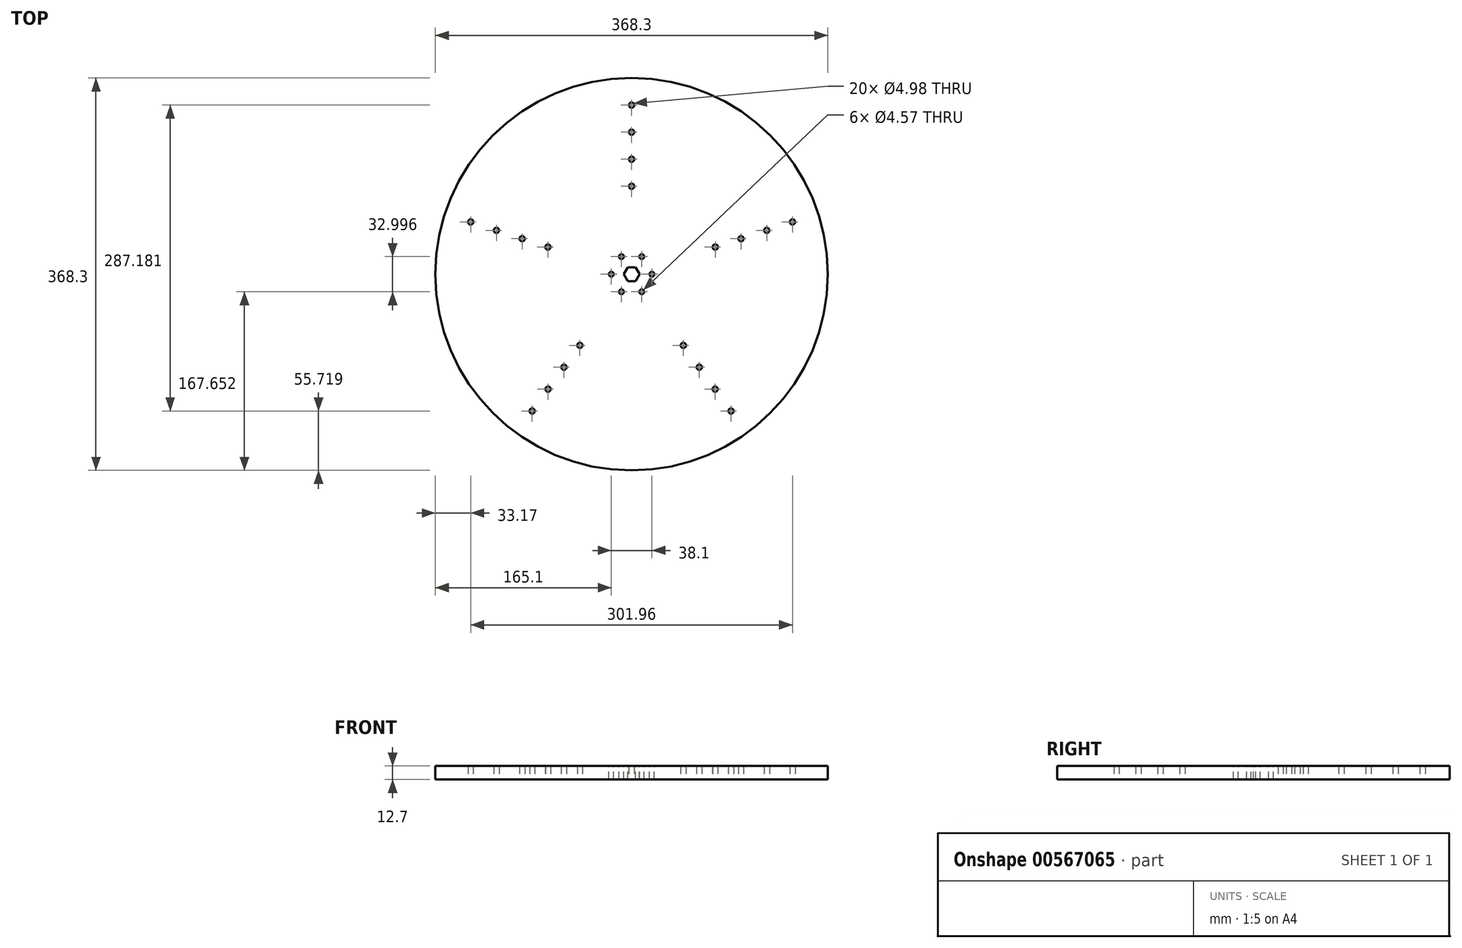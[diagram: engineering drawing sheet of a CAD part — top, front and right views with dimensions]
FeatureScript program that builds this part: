
annotation { "Feature Type Name" : "Feature", "Feature Type Description" : "" }
export const myFeature = defineFeature(function(context is Context, id is Id, definition is map)
    precondition{}
    {
        {
            var Q0;
            Q0=qCreatedBy(makeId("Top.planeOp"),FACE);
            var sketch = newSketch(context, id + "F0", { "sketchPlane" : qUnion([Q0])});
            skLineSegment(sketch, "E0", {"start": v(-174.54, 58.71) * mm, "end": v(-174.54, 58.71) * mm});
            skArc(sketch, "E1.cCircle", {"start": v(-174.54, 58.71) * mm, "mid": v(-175.72, -55.1) * mm, "end": v(-109.78, -147.85) * mm});
            skLineSegment(sketch, "E1.0", {"start": v(133.8, -184.15) * mm, "end": v(-133.8, -184.15) * mm, "construction": true});
            skLineSegment(sketch, "E1.1", {"start": v(-133.8, -184.15) * mm, "end": v(-216.48, 70.34) * mm, "construction": true});
            skLineSegment(sketch, "E1.2", {"start": v(-216.48, 70.34) * mm, "end": v(0, 227.62) * mm, "construction": true});
            skLineSegment(sketch, "E1.3", {"start": v(0, 227.62) * mm, "end": v(216.48, 70.34) * mm, "construction": true});
            skLineSegment(sketch, "E1.4", {"start": v(216.48, 70.34) * mm, "end": v(133.8, -184.15) * mm, "construction": true});
            skPoint(sketch, "E1.0.midPoint", {"position": v(0, -184.15) * mm});
            skLineSegment(sketch, "E2", {"start": v(0, 227.62) * mm, "end": v(0, 0) * mm, "construction": true});
            skLineSegment(sketch, "E3", {"start": v(-216.48, 70.34) * mm, "end": v(0, 0) * mm, "construction": true});
            skLineSegment(sketch, "E4", {"start": v(-133.8, -184.15) * mm, "end": v(0, 0) * mm, "construction": true});
            skLineSegment(sketch, "E5", {"start": v(133.8, -184.15) * mm, "end": v(0, 0) * mm, "construction": true});
            skLineSegment(sketch, "E6", {"start": v(216.48, 70.34) * mm, "end": v(0, 0) * mm, "construction": true});
            skLineSegment(sketch, "E7.bottom", {"start": v(1.9, 57.15) * mm, "end": v(-1.9, 57.15) * mm, "construction": true});
            skLineSegment(sketch, "E7.top", {"start": v(1.9, 209.55) * mm, "end": v(-1.9, 209.55) * mm, "construction": true});
            skLineSegment(sketch, "E7.left", {"start": v(1.9, 57.15) * mm, "end": v(1.9, 209.55) * mm, "construction": true});
            skLineSegment(sketch, "E7.right", {"start": v(-1.9, 57.15) * mm, "end": v(-1.9, 209.55) * mm, "construction": true});
            skArc(sketch, "E8.trimOffspring", {"start": v(-109.78, -147.85) * mm, "mid": v(175.72, 55.1) * mm, "end": v(-174.54, 58.71) * mm});
            skCircle(sketch, "E9", {"center": v(0, 82.55) * mm, "radius": 2.49 * mm});
            skCircle(sketch, "E10.0.1.0", {"center": v(0, 107.95) * mm, "radius": 2.49 * mm});
            skCircle(sketch, "E10.0.2.0", {"center": v(0, 133.35) * mm, "radius": 2.49 * mm});
            skLineSegment(sketch, "E10.direction1", {"start": v(0, 82.55) * mm, "end": v(25.4, 82.55) * mm, "construction": true});
            skLineSegment(sketch, "E10.direction2", {"start": v(0, 82.55) * mm, "end": v(0, 107.95) * mm, "construction": true});
            skCircle(sketch, "E11.0.0.3", {"center": v(0, 158.75) * mm, "radius": 2.49 * mm});
            skCircle(sketch, "E12.1.0", {"center": v(-78.5, 25.5) * mm, "radius": 2.49 * mm});
            skCircle(sketch, "E12.1.1", {"center": v(-102.67, 33.36) * mm, "radius": 2.49 * mm});
            skCircle(sketch, "E12.1.2", {"center": v(-126.82, 41.2) * mm, "radius": 2.49 * mm});
            skCircle(sketch, "E12.1.3", {"center": v(-150.98, 49.06) * mm, "radius": 2.49 * mm});
            skCircle(sketch, "E12.2.0", {"center": v(-48.52, -66.78) * mm, "radius": 2.49 * mm});
            skCircle(sketch, "E12.2.1", {"center": v(-63.45, -87.33) * mm, "radius": 2.49 * mm});
            skCircle(sketch, "E12.2.2", {"center": v(-78.38, -107.88) * mm, "radius": 2.49 * mm});
            skCircle(sketch, "E12.2.3", {"center": v(-93.31, -128.43) * mm, "radius": 2.49 * mm});
            skCircle(sketch, "E12.3.0", {"center": v(48.52, -66.78) * mm, "radius": 2.49 * mm});
            skCircle(sketch, "E12.3.1", {"center": v(63.45, -87.33) * mm, "radius": 2.49 * mm});
            skCircle(sketch, "E12.3.2", {"center": v(78.38, -107.88) * mm, "radius": 2.49 * mm});
            skCircle(sketch, "E12.3.3", {"center": v(93.31, -128.43) * mm, "radius": 2.49 * mm});
            skCircle(sketch, "E12.4.0", {"center": v(78.5, 25.5) * mm, "radius": 2.49 * mm});
            skCircle(sketch, "E12.4.1", {"center": v(102.67, 33.36) * mm, "radius": 2.49 * mm});
            skCircle(sketch, "E12.4.2", {"center": v(126.82, 41.2) * mm, "radius": 2.49 * mm});
            skCircle(sketch, "E12.4.3", {"center": v(150.98, 49.06) * mm, "radius": 2.49 * mm});
            skLineSegment(sketch, "E13", {"start": v(-1.9, 177.8) * mm, "end": v(1.9, 177.8) * mm, "construction": true});
            skSolve(sketch);
        }
        {
            var Q0;
            Q0=makeQuery(id+"F0.imprint","IMPRINT",FACE,{"disambiguationData":[TD([[makeQuery(id+"F0.imprint","IMPRINT",EDGE,{"derivedFrom":sQuery(id+"F0.wireOp",EDGE,"E1.cCircle")}),1.0]])]});
            extrude(context, id + "F1", {"entities" : qUnion([Q0]), "depth" : 12.7 * mm, "offsetDistance" : 25.4 * mm});
        }
        {
            var Q0;
            Q0=makeQuery(id+"F1.opExtrude","CAP_FACE",FACE,{"disambiguationData":[OSD([sQuery(id+"F0.wireOp",EDGE,"E1.cCircle"),sQuery(id+"F0.wireOp",EDGE,"E8.trimOffspring"),sQuery(id+"F0.wireOp",EDGE,"E9"),sQuery(id+"F0.wireOp",EDGE,"E10.0.1.0"),sQuery(id+"F0.wireOp",EDGE,"E10.0.2.0"),sQuery(id+"F0.wireOp",EDGE,"E11.0.0.3"),sQuery(id+"F0.wireOp",EDGE,"E12.1.0"),sQuery(id+"F0.wireOp",EDGE,"E12.1.1"),sQuery(id+"F0.wireOp",EDGE,"E12.1.2"),sQuery(id+"F0.wireOp",EDGE,"E12.1.3"),sQuery(id+"F0.wireOp",EDGE,"E12.2.0"),sQuery(id+"F0.wireOp",EDGE,"E12.2.1"),sQuery(id+"F0.wireOp",EDGE,"E12.2.2"),sQuery(id+"F0.wireOp",EDGE,"E12.2.3"),sQuery(id+"F0.wireOp",EDGE,"E12.3.0"),sQuery(id+"F0.wireOp",EDGE,"E12.3.1"),sQuery(id+"F0.wireOp",EDGE,"E12.3.2"),sQuery(id+"F0.wireOp",EDGE,"E12.3.3"),sQuery(id+"F0.wireOp",EDGE,"E12.4.0"),sQuery(id+"F0.wireOp",EDGE,"E12.4.1"),sQuery(id+"F0.wireOp",EDGE,"E12.4.2"),sQuery(id+"F0.wireOp",EDGE,"E12.4.3")])],"isStart":false});
            var sketch = newSketch(context, id + "F2", { "sketchPlane" : qUnion([Q0])});
            skCircle(sketch, "E14.cCircle", {"center": v(0, 0) * mm, "radius": 6.41 * mm, "construction": true});
            skLineSegment(sketch, "E14.0", {"start": v(-3.7, 6.41) * mm, "end": v(3.7, 6.41) * mm});
            skLineSegment(sketch, "E14.1", {"start": v(3.7, 6.41) * mm, "end": v(7.4, 0) * mm});
            skLineSegment(sketch, "E14.2", {"start": v(7.4, 0) * mm, "end": v(3.7, -6.41) * mm});
            skLineSegment(sketch, "E14.3", {"start": v(3.7, -6.41) * mm, "end": v(-3.7, -6.41) * mm});
            skLineSegment(sketch, "E14.4", {"start": v(-3.7, -6.41) * mm, "end": v(-7.4, 0) * mm});
            skLineSegment(sketch, "E14.5", {"start": v(-7.4, 0) * mm, "end": v(-3.7, 6.41) * mm});
            skPoint(sketch, "E14.0.midPoint", {"position": v(0, 6.41) * mm});
            skCircle(sketch, "E15", {"center": v(-19.05, 0) * mm, "radius": 2.29 * mm});
            skCircle(sketch, "E16.1.0", {"center": v(-9.53, -16.5) * mm, "radius": 2.29 * mm});
            skCircle(sketch, "E16.2.0", {"center": v(9.52, -16.5) * mm, "radius": 2.29 * mm});
            skCircle(sketch, "E16.3.0", {"center": v(19.05, 0) * mm, "radius": 2.29 * mm});
            skCircle(sketch, "E16.4.0", {"center": v(9.53, 16.5) * mm, "radius": 2.29 * mm});
            skCircle(sketch, "E16.5.0", {"center": v(-9.52, 16.5) * mm, "radius": 2.29 * mm});
            skSolve(sketch);
        }
        {
            var Q0;
            Q0=qSketchRegion(id+"F2",true);
            var Q1;
            Q1=makeQuery(id+"F1.opExtrude","CAP_FACE",FACE,{"disambiguationData":[OSD([sQuery(id+"F0.wireOp",EDGE,"E1.cCircle"),sQuery(id+"F0.wireOp",EDGE,"E8.trimOffspring"),sQuery(id+"F0.wireOp",EDGE,"E9"),sQuery(id+"F0.wireOp",EDGE,"E10.0.1.0"),sQuery(id+"F0.wireOp",EDGE,"E10.0.2.0"),sQuery(id+"F0.wireOp",EDGE,"E11.0.0.3"),sQuery(id+"F0.wireOp",EDGE,"E12.1.0"),sQuery(id+"F0.wireOp",EDGE,"E12.1.1"),sQuery(id+"F0.wireOp",EDGE,"E12.1.2"),sQuery(id+"F0.wireOp",EDGE,"E12.1.3"),sQuery(id+"F0.wireOp",EDGE,"E12.2.0"),sQuery(id+"F0.wireOp",EDGE,"E12.2.1"),sQuery(id+"F0.wireOp",EDGE,"E12.2.2"),sQuery(id+"F0.wireOp",EDGE,"E12.2.3"),sQuery(id+"F0.wireOp",EDGE,"E12.3.0"),sQuery(id+"F0.wireOp",EDGE,"E12.3.1"),sQuery(id+"F0.wireOp",EDGE,"E12.3.2"),sQuery(id+"F0.wireOp",EDGE,"E12.3.3"),sQuery(id+"F0.wireOp",EDGE,"E12.4.0"),sQuery(id+"F0.wireOp",EDGE,"E12.4.1"),sQuery(id+"F0.wireOp",EDGE,"E12.4.2"),sQuery(id+"F0.wireOp",EDGE,"E12.4.3")])],"isStart":true});
            extrude(context, id + "F3", {"entities" : qUnion([Q0]), "operationType" : NewBodyOperationType.REMOVE, "endBound" : BoundingType.UP_TO_SURFACE, "oppositeDirection" : true, "endBoundEntityFace" : qUnion([Q1]), "depth" : 25.4 * mm, "offsetDistance" : 25.4 * mm});
        }
    });
